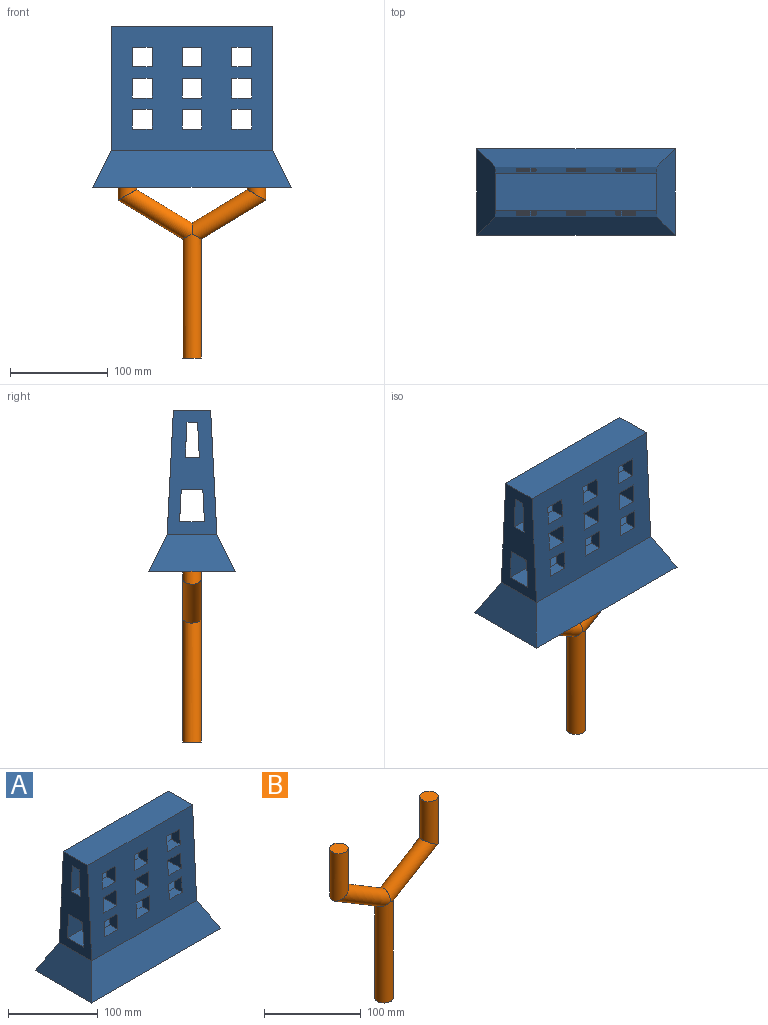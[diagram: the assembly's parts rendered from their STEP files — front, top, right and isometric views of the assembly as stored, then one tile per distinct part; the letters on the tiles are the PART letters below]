
ASSEMBLY  parts=2 mates=1
PART A: 82 faces, bbox 203.2x88.9x165.1 mm
  f0: plane 20.32x13.99mm, normal (0,0,-1), area 284.2mm2, adj f1,f3,f32,f78
  f1: plane 20.32x15mm, normal (1,0,0), area 284.2mm2, adj f0,f2,f32,f78
  f2: plane 20.32x13.99mm, normal (0,0,1), area 284.2mm2, adj f1,f3,f32,f78
  f3: plane 20.32x15mm, normal (-1,0,0), area 284.2mm2, adj f0,f2,f32,f78
  f4: plane 20.32x12.05mm, normal (0,0,-1), area 244.9mm2, adj f5,f7,f32,f74
  f5: plane 20.32x13.07mm, normal (1,0,0), area 244.9mm2, adj f4,f6,f32,f74
  f6: plane 20.32x12.05mm, normal (0,0,1), area 244.9mm2, adj f5,f7,f32,f74
  f7: plane 20.32x13.07mm, normal (-1,0,0), area 244.9mm2, adj f4,f6,f32,f74
  f8: plane 20.32x13.99mm, normal (0,0,-1), area 284.2mm2, adj f9,f11,f32,f78
  f9: plane 20.32x15mm, normal (1,0,0), area 284.2mm2, adj f8,f10,f32,f78
  f10: plane 20.32x13.99mm, normal (0,0,1), area 284.2mm2, adj f9,f11,f32,f78
  f11: plane 20.32x15mm, normal (-1,0,0), area 284.2mm2, adj f8,f10,f32,f78
  f12: plane 20.32x12.05mm, normal (0,0,-1), area 244.9mm2, adj f13,f15,f32,f74
  f13: plane 20.32x13.07mm, normal (1,0,0), area 244.9mm2, adj f12,f14,f32,f74
  f14: plane 20.32x12.05mm, normal (0,0,1), area 244.9mm2, adj f13,f15,f32,f74
  f15: plane 20.32x13.07mm, normal (-1,0,0), area 244.9mm2, adj f12,f14,f32,f74
  f16: plane 20.32x13.99mm, normal (0,0,-1), area 284.2mm2, adj f17,f19,f32,f78
  f17: plane 20.32x15mm, normal (1,0,0), area 284.2mm2, adj f16,f18,f32,f78
  f18: plane 20.32x13.99mm, normal (0,0,1), area 284.2mm2, adj f17,f19,f32,f78
  f19: plane 20.32x15mm, normal (-1,0,0), area 284.2mm2, adj f16,f18,f32,f78
  f20: plane 20.32x12.05mm, normal (0,0,-1), area 244.9mm2, adj f21,f23,f32,f74
  f21: plane 20.32x13.07mm, normal (1,0,0), area 244.9mm2, adj f20,f22,f32,f74
  f22: plane 20.32x12.05mm, normal (0,0,1), area 244.9mm2, adj f21,f23,f32,f74
  f23: plane 20.32x13.07mm, normal (-1,0,0), area 244.9mm2, adj f20,f22,f32,f74
  f24: plane 165.1x127mm, normal (0,1,0.05), area 17273.1mm2, adj f29,f30,f31,f33,f34,f35,f36,f37
  f25: plane 203.2x88.9mm, normal (0,0,-1), area 17494.4mm2, adj f26,f27,f28,f29,f70,f72
  f26: plane 88.9x38.1mm, normal (-0.89,0,0.45), area 2975.4mm2, adj f25,f27,f29,f31
  f27: plane 203.2x38.1mm, normal (0,-0.89,0.45), area 7844.3mm2, adj f25,f26,f28,f32
  f28: plane 88.9x38.1mm, normal (0.89,0,0.45), area 2975.4mm2, adj f25,f27,f29,f33
  f29: plane 203.2x38.1mm, normal (0,0.89,0.45), area 7844.3mm2, adj f24,f25,f26,f28
  f30: plane 165.1x38.1mm, normal (0,0,1), area 6290.3mm2, adj f24,f31,f32,f33
  f31: plane 127x50.8mm, normal (-1,0,0), area 4412mm2, adj f24,f26,f30,f32,f74,f75,f76,f77
  f32: plane 165.1x127mm, normal (0,-1,0.05), area 17273.1mm2, adj f0,f1,f2,f3,f4,f5,f6,f7
  f33: plane 127x50.8mm, normal (1,0,0), area 4412mm2, adj f24,f28,f30,f32,f74,f75,f76,f77
  f34: plane 20.32x14.53mm, normal (0,0,-1), area 295.3mm2, adj f24,f35,f37,f80
  f35: plane 20.32x15.55mm, normal (1,0,0), area 295.3mm2, adj f24,f34,f36,f80
  f36: plane 20.32x14.53mm, normal (0,0,1), area 295.3mm2, adj f24,f35,f37,f80
  f37: plane 20.32x15.55mm, normal (-1,0,0), area 295.3mm2, adj f24,f34,f36,f80
  f38: plane 20.32x12.08mm, normal (0,0,-1), area 245.5mm2, adj f24,f39,f41,f76
  f39: plane 20.32x13.1mm, normal (1,0,0), area 245.5mm2, adj f24,f38,f40,f76
  f40: plane 20.32x12.08mm, normal (0,0,1), area 245.5mm2, adj f24,f39,f41,f76
  f41: plane 20.32x13.1mm, normal (-1,0,0), area 245.5mm2, adj f24,f38,f40,f76
  f42: plane 20.32x14.53mm, normal (0,0,-1), area 295.3mm2, adj f24,f43,f45,f80
  f43: plane 20.32x15.55mm, normal (1,0,0), area 295.3mm2, adj f24,f42,f44,f80
  f44: plane 20.32x14.53mm, normal (0,0,1), area 295.3mm2, adj f24,f43,f45,f80
  f45: plane 20.32x15.55mm, normal (-1,0,0), area 295.3mm2, adj f24,f42,f44,f80
  f46: plane 43.43x20.32mm, normal (0,0,-1), area 882.6mm2, adj f24,f32,f47,f49
  f47: plane 45.47x20.32mm, normal (1,0,0), area 903.2mm2, adj f24,f32,f46,f48
  f48: plane 45.47x20.32mm, normal (0,0,1), area 923.9mm2, adj f24,f32,f47,f49
  f49: plane 45.47x20.32mm, normal (-1,0,0), area 903.2mm2, adj f24,f32,f46,f48
  f50: plane 20.32x12.08mm, normal (0,0,-1), area 245.5mm2, adj f24,f51,f53,f76
  f51: plane 20.32x13.1mm, normal (1,0,0), area 245.5mm2, adj f24,f50,f52,f76
  f52: plane 20.32x12.08mm, normal (0,0,1), area 245.5mm2, adj f24,f51,f53,f76
  f53: plane 20.32x13.1mm, normal (-1,0,0), area 245.5mm2, adj f24,f50,f52,f76
  f54: plane 43.43x20.32mm, normal (0,0,-1), area 882.6mm2, adj f24,f32,f55,f57
  f55: plane 45.47x20.32mm, normal (1,0,0), area 903.2mm2, adj f24,f32,f54,f56
  f56: plane 45.47x20.32mm, normal (0,0,1), area 923.9mm2, adj f24,f32,f55,f57
  f57: plane 45.47x20.32mm, normal (-1,0,0), area 903.2mm2, adj f24,f32,f54,f56
  f58: plane 20.32x14.53mm, normal (0,0,-1), area 295.3mm2, adj f24,f59,f61,f80
  f59: plane 20.32x15.55mm, normal (1,0,0), area 295.3mm2, adj f24,f58,f60,f80
  f60: plane 20.32x14.53mm, normal (0,0,1), area 295.3mm2, adj f24,f59,f61,f80
  f61: plane 20.32x15.55mm, normal (-1,0,0), area 295.3mm2, adj f24,f58,f60,f80
  f62: plane 20.32x12.08mm, normal (0,0,-1), area 245.5mm2, adj f24,f63,f65,f76
  f63: plane 20.32x13.1mm, normal (1,0,0), area 245.5mm2, adj f24,f62,f64,f76
  f64: plane 20.32x12.08mm, normal (0,0,1), area 245.5mm2, adj f24,f63,f65,f76
  f65: plane 20.32x13.1mm, normal (-1,0,0), area 245.5mm2, adj f24,f62,f64,f76
  f66: plane 43.43x20.32mm, normal (0,0,-1), area 882.6mm2, adj f24,f32,f67,f69
  f67: plane 45.47x20.32mm, normal (1,0,0), area 903.2mm2, adj f24,f32,f66,f68
  f68: plane 45.47x20.32mm, normal (0,0,1), area 923.9mm2, adj f24,f32,f67,f69
  f69: plane 45.47x20.32mm, normal (-1,0,0), area 903.2mm2, adj f24,f32,f66,f68
  f70: cylinder r=9.53mm len=48.26mm, axis (0,0,-1), area 2888.2mm2, adj f25,f71
  f71: plane 19.05x19.05mm, normal (0,0,-1), area 285mm2, adj f70
  f72: cylinder r=9.53mm len=48.26mm, axis (0,0,-1), area 2888.2mm2, adj f25,f73
  f73: plane 19.05x19.05mm, normal (0,0,-1), area 285mm2, adj f72
  f74: plane 165.1x33.02mm, normal (0,1,-0.05), area 4218.2mm2, adj f4,f5,f6,f7,f12,f13,f14,f15
  f75: plane 165.1x25.4mm, normal (0,0,1), area 4193.5mm2, adj f31,f33,f74,f76
  f76: plane 165.1x33.02mm, normal (0,-1,-0.05), area 4218.2mm2, adj f31,f33,f38,f39,f40,f41,f50,f51
  f77: plane 165.1x22.1mm, normal (0,0,-1), area 3648.4mm2, adj f31,f33,f74,f76
  f78: plane 165.1x35.56mm, normal (0,1,-0.05), area 4638mm2, adj f0,f1,f2,f3,f8,f9,f10,f11
  f79: plane 165.1x14.4mm, normal (0,0,1), area 2378.1mm2, adj f31,f33,f78,f80
  f80: plane 165.1x35.56mm, normal (0,-1,-0.05), area 4638mm2, adj f31,f33,f34,f35,f36,f37,f42,f43
  f81: plane 165.1x10.85mm, normal (0,0,-1), area 1791mm2, adj f31,f33,f78,f80
PART B: 8 faces, bbox 151.1x19.1x222.6 mm
  f0: plane 19.05x19.05mm, normal (0,0,1), area 285mm2, adj f2
  f1: plane 19.05x19.05mm, normal (0,0,-1), area 285mm2, adj f4
  f2: cylinder r=9.53mm len=61.27mm, axis (0,0,1), area 3344.3mm2, adj f0,f3
  f3: cylinder r=9.53mm len=80.47mm, axis (-0.86,0,0.52), area 4423.6mm2, adj f2,f4,f7
  f4: cylinder r=9.53mm len=127mm, axis (0,0,1), area 7417.4mm2, adj f1,f3,f7
  f5: plane 19.05x19.05mm, normal (0,0,1), area 285mm2, adj f6
  f6: cylinder r=9.53mm len=61.27mm, axis (0,0,1), area 3344.3mm2, adj f5,f7
  f7: cylinder r=9.53mm len=80.48mm, axis (0.86,0,0.52), area 4445.6mm2, adj f3,f4,f6
PLACE A t=(-97.09,-18.57,-0.73)mm
PLACE B t=(-97.09,-18.57,-48.06)mm
MATE fastened B.f2 <-> A.f72  axis (0,0,1) through (-163.13,-18.57,47.53)mm
